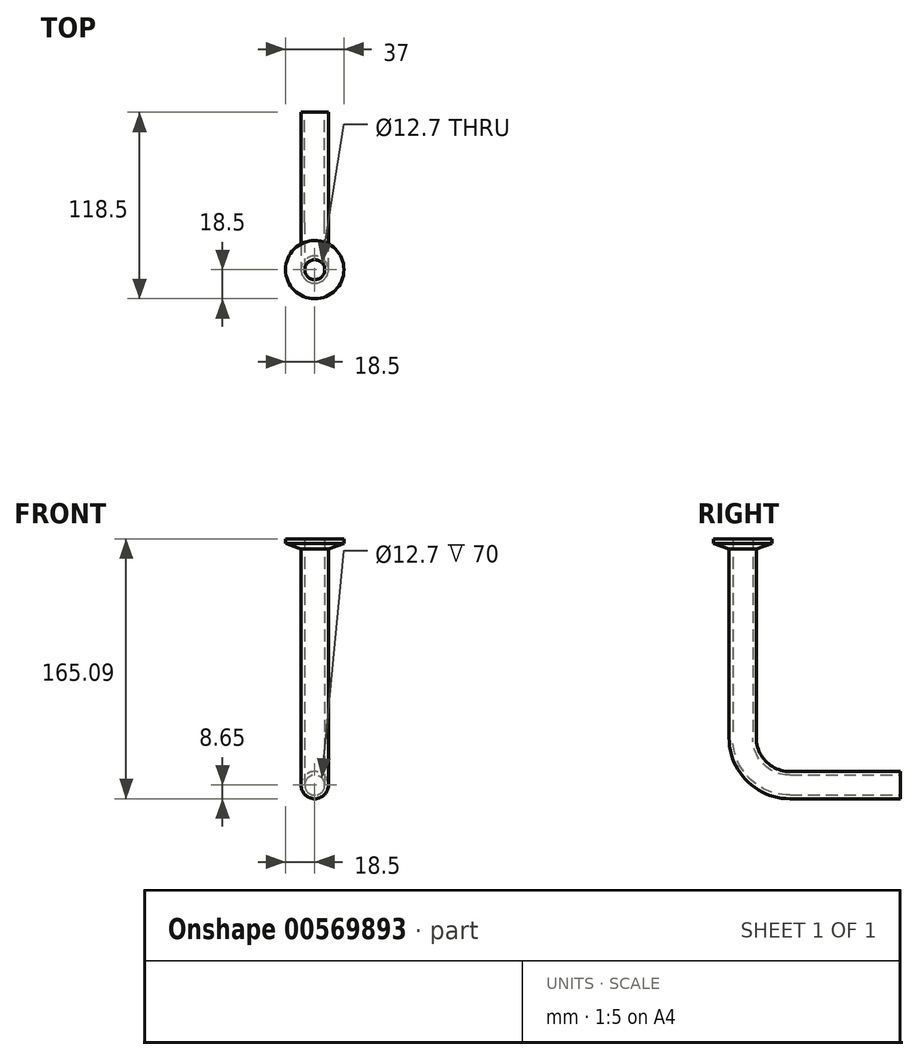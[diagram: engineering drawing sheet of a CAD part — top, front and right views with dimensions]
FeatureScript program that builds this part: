
annotation { "Feature Type Name" : "Feature", "Feature Type Description" : "" }
export const myFeature = defineFeature(function(context is Context, id is Id, definition is map)
    precondition{}
    {
        {
            var Q0;
            Q0=qCreatedBy(makeId("Front.planeOp"),FACE);
            var sketch = newSketch(context, id + "F0", { "sketchPlane" : qUnion([Q0])});
            skLineSegment(sketch, "E0", {"start": v(6.35, 0) * mm, "end": v(6.35, 6.44) * mm});
            skLineSegment(sketch, "E1", {"start": v(6.35, 6.44) * mm, "end": v(18.5, 6.44) * mm});
            skLineSegment(sketch, "E2", {"start": v(18.5, 6.44) * mm, "end": v(18.5, 3.59) * mm});
            skLineSegment(sketch, "E3", {"start": v(18.5, 3.59) * mm, "end": v(8.65, 0) * mm});
            skLineSegment(sketch, "E4", {"start": v(8.65, 0) * mm, "end": v(6.35, 0) * mm});
            skLineSegment(sketch, "E5", {"start": v(0, 0) * mm, "end": v(0, 11.29) * mm, "construction": true});
            skSolve(sketch);
        }
        {
            var Q0;
            Q0=qSketchRegion(id+"F0",true);
            var Q1;
            Q1=sQuery(id+"F0.wireOp",EDGE,"E5");
            revolve(context, id + "F1", {"entities" : qUnion([Q0]), "axis" : qUnion([Q1]), "revolveType" : RevolveType.FULL});
        }
        {
            var Q0;
            Q0=qCreatedBy(makeId("Top.planeOp"),FACE);
            var sketch = newSketch(context, id + "F2", { "sketchPlane" : qUnion([Q0])});
            skCircle(sketch, "E6", {"center": v(0, 0) * mm, "radius": 8.65 * mm});
            skCircle(sketch, "E7", {"center": v(0, 0) * mm, "radius": 6.35 * mm});
            skSolve(sketch);
        }
        {
            var Q0;
            Q0=qCreatedBy(makeId("Right.planeOp"),FACE);
            var sketch = newSketch(context, id + "F3", { "sketchPlane" : qUnion([Q0])});
            skLineSegment(sketch, "E8", {"start": v(0, 0) * mm, "end": v(0, -120) * mm});
            skLineSegment(sketch, "E9", {"start": v(30, -150) * mm, "end": v(100, -150) * mm});
            skPoint(sketch, "E10.visualSharp", {"position": v(0, -150) * mm});
            skArc(sketch, "E10.filletArc", {"start": v(0, -120) * mm, "mid": v(8.79, -141.21) * mm, "end": v(30, -150) * mm});
            skSolve(sketch);
        }
        {
            var Q0;
            Q0 = qSketchRegion(id + "F2", true);
            var Q1;
            Q1 = qConstructionFilter(qBodyType(qCreatedBy(id + "F3" ,EDGE), BodyType.WIRE), ConstructionObject.NO);
            sweep(context, id + "F4", {"operationType" : NewBodyOperationType.ADD, "profiles" : qUnion([Q0]), "path" : qUnion([Q1])});
        }
    });
